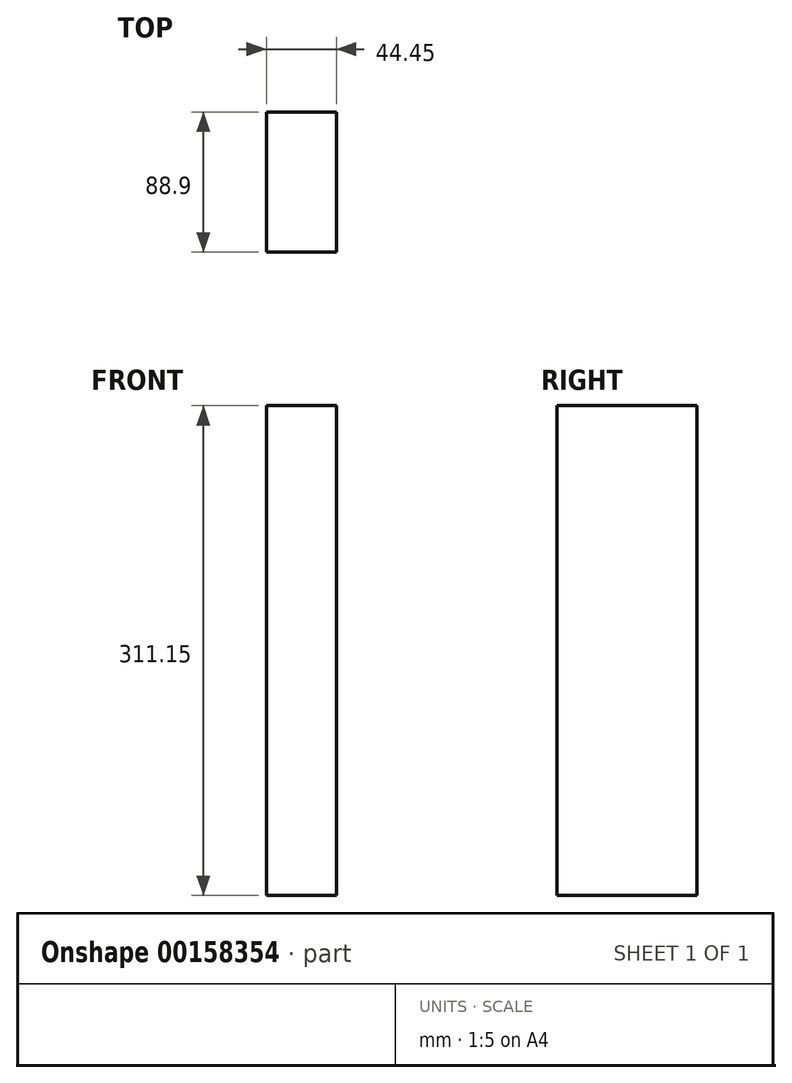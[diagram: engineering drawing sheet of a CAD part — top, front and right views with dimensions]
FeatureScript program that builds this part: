
annotation { "Feature Type Name" : "Feature", "Feature Type Description" : "" }
export const myFeature = defineFeature(function(context is Context, id is Id, definition is map)
    precondition{}
    {
        {
            var Q0;
            Q0=qCreatedBy(makeId("Front.planeOp"),FACE);
            var sketch = newSketch(context, id + "F0", { "sketchPlane" : qUnion([Q0])});
            skLineSegment(sketch, "E0", {"start": v(-50.51, 153.15) * mm, "end": v(-50.51, -158) * mm});
            skSolve(sketch);
        }
        {
            var Q0;
            Q0=sQuery(id+"F0.wireOp",EDGE,"E0");
            extrude(context, id + "F1", {"bodyType" : ToolBodyType.SURFACE, "surfaceEntities" : qUnion([Q0]), "endBound" : BoundingType.SYMMETRIC, "depth" : 88.9 * mm});
        }
        {
            var Q0;
            Q0=makeQuery(id+"F1.opExtrude","SWEPT_FACE",FACE,{"disambiguationData":[OSD([sQuery(id+"F0.wireOp",EDGE,"E0")])]});
            extrude(context, id + "F2", {"entities" : qUnion([Q0]), "depth" : 44.45 * mm});
        }
    });
